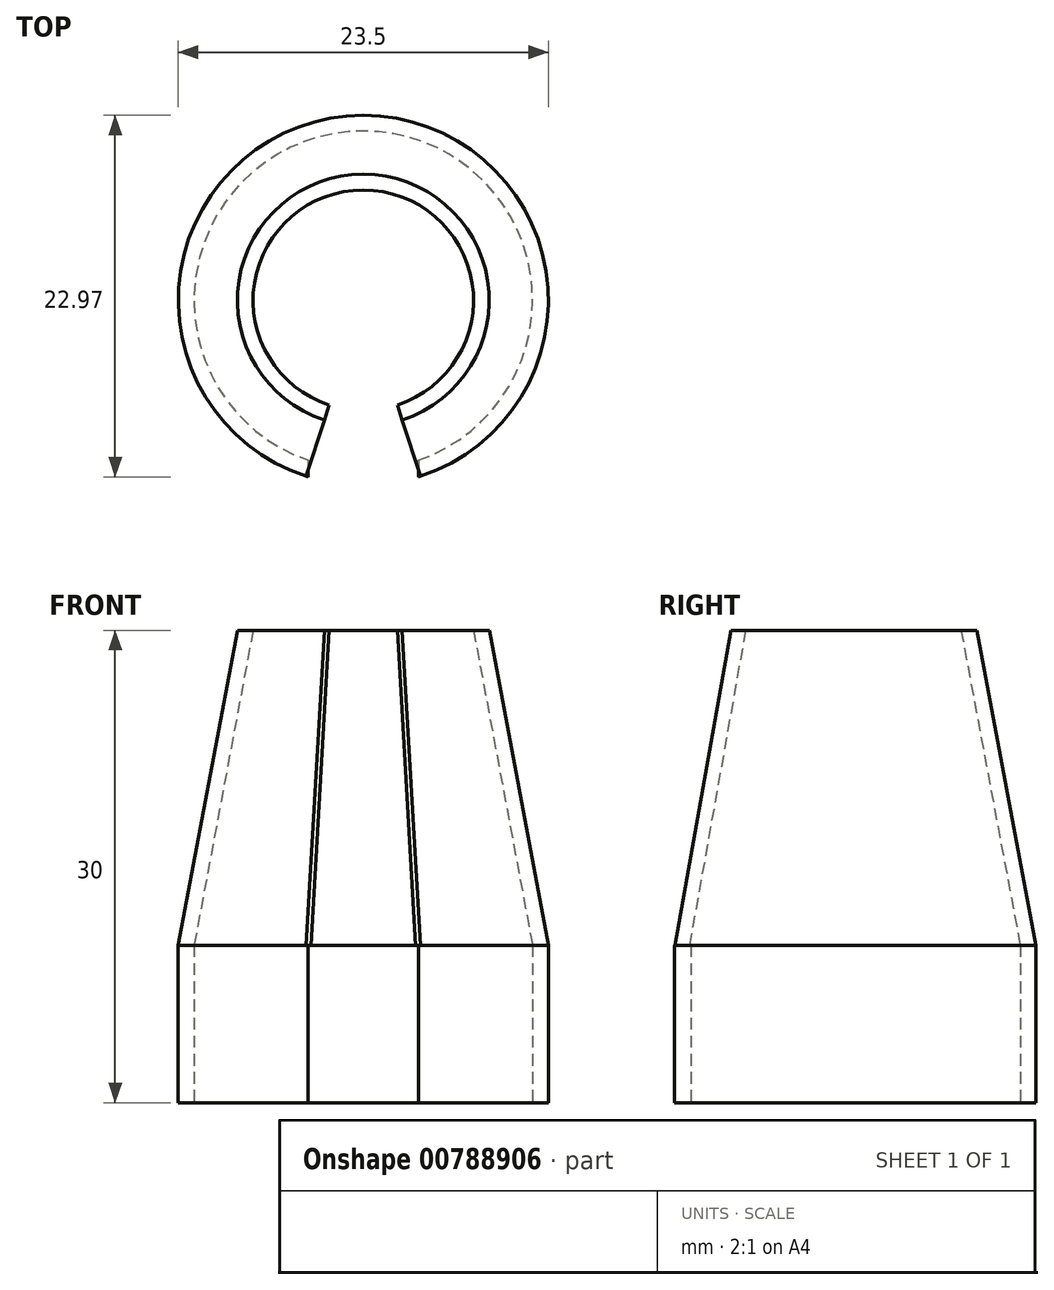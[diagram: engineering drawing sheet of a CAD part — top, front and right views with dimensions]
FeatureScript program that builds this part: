
annotation { "Feature Type Name" : "Feature", "Feature Type Description" : "" }
export const myFeature = defineFeature(function(context is Context, id is Id, definition is map)
    precondition{}
    {
        {
            var Q0;
            Q0=qCreatedBy(makeId("Top.planeOp"),FACE);
            var sketch = newSketch(context, id + "F0", { "sketchPlane" : qUnion([Q0])});
            skArc(sketch, "E0", {"start": v(3.5, -10.16) * mm, "mid": v(0, 10.75) * mm, "end": v(-3.5, -10.16) * mm});
            skArc(sketch, "E1", {"start": v(3.5, -11.22) * mm, "mid": v(0, 11.75) * mm, "end": v(-3.5, -11.22) * mm});
            skLineSegment(sketch, "E2.top", {"start": v(-3.5, -14.85) * mm, "end": v(3.5, -14.85) * mm});
            skLineSegment(sketch, "E2.left", {"start": v(-3.5, -10.16) * mm, "end": v(-3.5, -11.22) * mm});
            skLineSegment(sketch, "E2.right", {"start": v(3.5, -10.16) * mm, "end": v(3.5, -11.22) * mm});
            skPoint(sketch, "E3.orphan", {"position": v(3.5, 0) * mm});
            skPoint(sketch, "E2.bottom.start.orphan", {"position": v(-3.5, 0) * mm});
            skSolve(sketch);
        }
        {
            var Q0;
            Q0 = qSketchRegion(id + "F0", true);
            extrude(context, id + "F1", {"entities" : qUnion([Q0]), "depth" : 10 * mm, "offsetDistance" : 25 * mm});
        }
        {
            var Q0;
            Q0=qCreatedBy(makeId("Front.planeOp"),FACE);
            var sketch = newSketch(context, id + "F2", { "sketchPlane" : qUnion([Q0])});
            skLineSegment(sketch, "E4.0.0", {"start": v(-11.75, 0) * mm, "end": v(11.75, 0) * mm});
            skLineSegment(sketch, "E4.0.1", {"start": v(-3.5, 0) * mm, "end": v(-3.5, 10) * mm});
            skLineSegment(sketch, "E4.0.3", {"start": v(3.5, 10) * mm, "end": v(3.5, 0) * mm});
            skLineSegment(sketch, "E5", {"start": v(0, 0) * mm, "end": v(0, 62.74) * mm, "construction": true});
            skLineSegment(sketch, "E6.0", {"start": v(-11.75, 10) * mm, "end": v(11.75, 10) * mm});
            skLineSegment(sketch, "E7", {"start": v(-7, 10) * mm, "end": v(-7, 34.75) * mm, "construction": true});
            skLineSegment(sketch, "E8.0", {"start": v(-10.75, 10) * mm, "end": v(10.75, 10) * mm});
            skLineSegment(sketch, "E9", {"start": v(-10.75, 10) * mm, "end": v(-7, 30) * mm});
            skLineSegment(sketch, "E10", {"start": v(-8, 30) * mm, "end": v(-11.75, 10) * mm});
            skLineSegment(sketch, "E11", {"start": v(-7, 30) * mm, "end": v(-8, 30) * mm});
            skSolve(sketch);
        }
        {
            var Q0;
            {var subQ0=sQuery(id+"F2.wireOp",EDGE,"E9");Q0=makeQuery(id+"F2.imprint","IMPRINT",FACE,{"disambiguationData":[TD([[makeQuery(id+"F2.imprint","IMPRINT",EDGE,{"derivedFrom":subQ0}),1.0]])]});}
            var Q1;
            Q1=sQuery(id+"F2.wireOp",EDGE,"E5");
            revolve(context, id + "F3", {"operationType" : NewBodyOperationType.ADD, "surfaceOperationType" : NewSurfaceOperationType.NEW, "entities" : qUnion([Q0]), "axis" : qUnion([Q1]), "revolveType" : RevolveType.TWO_DIRECTIONS, "angle" : 72 * degree, "angleBack" : 108 * degree});
        }
    });
